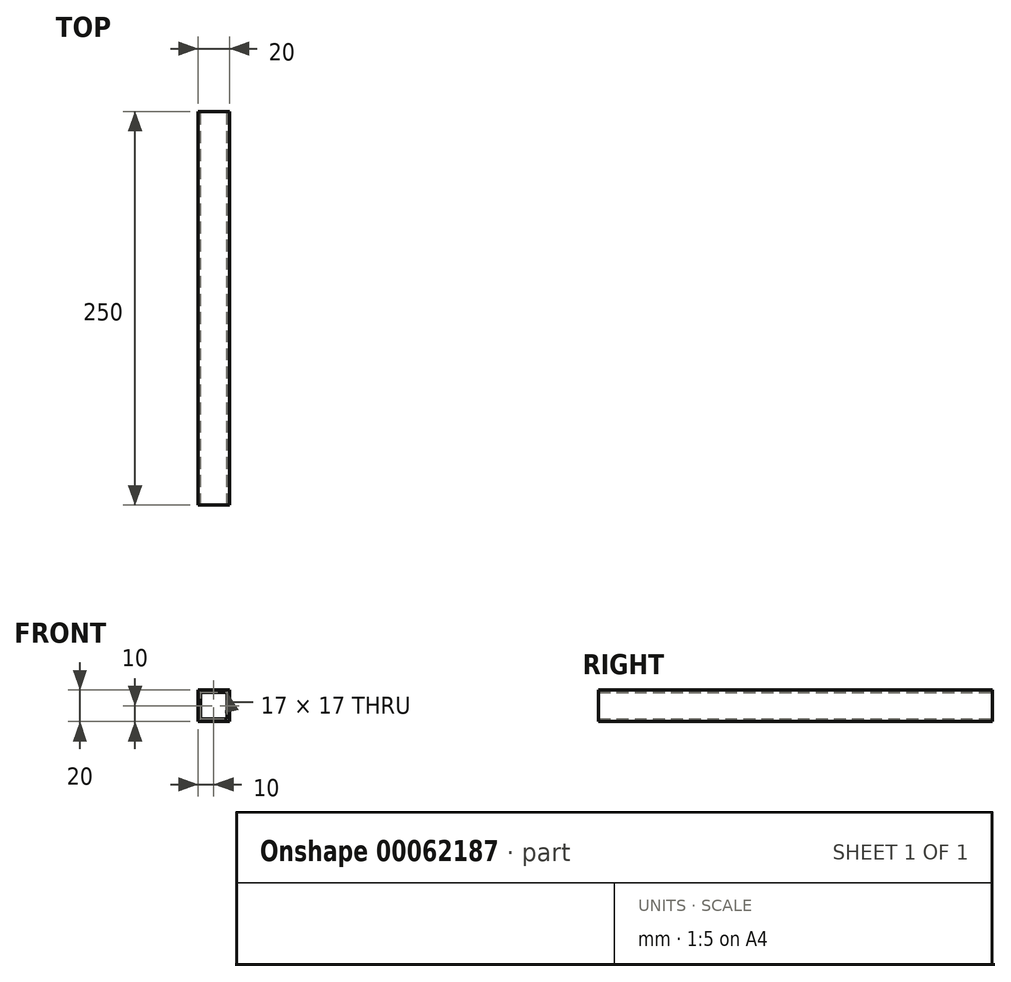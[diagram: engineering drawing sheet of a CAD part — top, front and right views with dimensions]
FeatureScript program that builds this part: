
annotation { "Feature Type Name" : "Feature", "Feature Type Description" : "" }
export const myFeature = defineFeature(function(context is Context, id is Id, definition is map)
    precondition{}
    {
        {
            var Q0;
            Q0=qCreatedBy(makeId("Front.planeOp"),FACE);
            var sketch = newSketch(context, id + "F0", { "sketchPlane" : qUnion([Q0])});
            skLineSegment(sketch, "E0.bottom", {"start": v(0, 0) * mm, "end": v(20, 0) * mm});
            skLineSegment(sketch, "E0.top", {"start": v(0, 20) * mm, "end": v(20, 20) * mm});
            skLineSegment(sketch, "E0.left", {"start": v(0, 0) * mm, "end": v(0, 20) * mm});
            skLineSegment(sketch, "E0.right", {"start": v(20, 0) * mm, "end": v(20, 20) * mm});
            skLineSegment(sketch, "E1.0", {"start": v(18.5, 1.5) * mm, "end": v(18.5, 18.5) * mm});
            skLineSegment(sketch, "E1.1", {"start": v(1.5, 1.5) * mm, "end": v(18.5, 1.5) * mm});
            skLineSegment(sketch, "E1.2", {"start": v(1.5, 1.5) * mm, "end": v(1.5, 18.5) * mm});
            skLineSegment(sketch, "E1.3", {"start": v(1.5, 18.5) * mm, "end": v(18.5, 18.5) * mm});
            skSolve(sketch);
        }
        {
            var Q0;
            Q0=qSketchRegion(id+"F0",true);
            extrude(context, id + "F1", {"entities" : qUnion([Q0]), "depth" : 250 * mm});
        }
    });
